annotation { "Feature Type Name" : "Feature", "Feature Type Description" : "" }
export const myFeature = defineFeature(function(context is Context, id is Id, definition is map)
    precondition{}
    {
        {
            var Q0;
            Q0=qCreatedBy(makeId("Top.planeOp"),FACE);
            var sketch = newSketch(context, id + "F0", { "sketchPlane" : qUnion([Q0])});
            skLineSegment(sketch, "E0.left", {"start": v(152.4, 161.9) * mm, "end": v(152.4, -3.62) * mm});
            skLineSegment(sketch, "E0.right", {"start": v(-152.4, 161.9) * mm, "end": v(-152.4, -3.62) * mm});
            skPoint(sketch, "E0.middle", {"position": v(0, 0) * mm});
            skLineSegment(sketch, "E1", {"start": v(-88.9, 201.69) * mm, "end": v(0, 230.34) * mm});
            skLineSegment(sketch, "E2", {"start": v(0, 230.34) * mm, "end": v(0, 0) * mm, "construction": true});
            skLineSegment(sketch, "E3.MirrorCS", {"start": v(88.9, 201.69) * mm, "end": v(0, 230.34) * mm});
            skPoint(sketch, "E4.orphan", {"position": v(-88.9, 201.69) * mm});
            skPoint(sketch, "E0.bottom.end.orphan", {"position": v(88.9, 201.69) * mm});
            skPoint(sketch, "E5.orphan", {"position": v(152.4, 236.65) * mm});
            skArc(sketch, "E6", {"start": v(-152.4, -3.62) * mm, "mid": v(-110.76, -140.2) * mm, "end": v(0, -230.34) * mm});
            skArc(sketch, "E7.MirrorCS", {"start": v(152.4, -3.62) * mm, "mid": v(110.76, -140.2) * mm, "end": v(0, -230.34) * mm});
            skPoint(sketch, "E8.orphan", {"position": v(-152.4, -236.65) * mm});
            skPoint(sketch, "E9.orphan", {"position": v(152.4, -224.03) * mm});
            skPoint(sketch, "E10.orphan", {"position": v(-152.4, 181.18) * mm});
            skPoint(sketch, "E11.center.orphan", {"position": v(-152.4, 224.03) * mm});
            skPoint(sketch, "E12.MirrorCS.center.orphan", {"position": v(147.26, 182.37) * mm});
            skArc(sketch, "E13", {"start": v(-113.58, 176.71) * mm, "mid": v(-98.53, 186.52) * mm, "end": v(-88.9, 201.69) * mm});
            skArc(sketch, "E14.MirrorCS", {"start": v(113.58, 176.71) * mm, "mid": v(98.53, 186.52) * mm, "end": v(88.9, 201.69) * mm});
            skLineSegment(sketch, "E15", {"start": v(-152.4, 161.9) * mm, "end": v(-113.58, 176.71) * mm});
            skLineSegment(sketch, "E16.MirrorCS", {"start": v(152.4, 161.9) * mm, "end": v(113.58, 176.71) * mm});
            skPoint(sketch, "E17.orphan", {"position": v(152.4, 181.18) * mm});
            skSolve(sketch);
        }
        {
            var Q0;
            Q0=makeQuery(id+"F0.imprint","IMPRINT",FACE,{"disambiguationData":[TD([[makeQuery(id+"F0.imprint","IMPRINT",EDGE,{"derivedFrom":sQuery(id+"F0.wireOp",EDGE,"E0.left")}),-1.0]])]});
            extrude(context, id + "F1", {"entities" : qUnion([Q0]), "depth" : 25.4 * mm, "offsetDistance" : 25.4 * mm});
        }
        {
            var Q0;
            Q0=makeQuery(id+"F1.opExtrude","CAP_FACE",FACE,{"disambiguationData":[OSD([sQuery(id+"F0.wireOp",EDGE,"E0.left"),sQuery(id+"F0.wireOp",EDGE,"E0.right"),sQuery(id+"F0.wireOp",EDGE,"E1"),sQuery(id+"F0.wireOp",EDGE,"E3.MirrorCS"),sQuery(id+"F0.wireOp",EDGE,"E6"),sQuery(id+"F0.wireOp",EDGE,"E7.MirrorCS"),sQuery(id+"F0.wireOp",EDGE,"E13"),sQuery(id+"F0.wireOp",EDGE,"E14.MirrorCS"),sQuery(id+"F0.wireOp",EDGE,"E15"),sQuery(id+"F0.wireOp",EDGE,"E16.MirrorCS")])],"isStart":false});
            var sketch = newSketch(context, id + "F2", { "sketchPlane" : qUnion([Q0])});
            skText(sketch, "E18", { "text": "THANK YOU ", "fontName": "RobotoSlab-Regular.ttf"});
            skText(sketch, "E19", { "text": "FOR YOUR DEDICATION", "fontName": "OpenSans-Bold.ttf"});
            skText(sketch, "E20", { "text": "GLENN DODGE", "fontName": "RobotoSlab-Bold.ttf"});
            skText(sketch, "E21", { "text": "501", "fontName": "RobotoSlab-Bold.ttf"});
            skText(sketch, "E22", { "text": "PK", "fontName": "RobotoSlab-Bold.ttf"});
            const initialGuessF2  = {"E18": [-0.13322, 0.12096, 1, 0, 0.03185], "E19": [-0.13322, 0.09164, 1, 0, 0.01662], "E20": [-0.13322, 0.0518, 1, 0, 0.02715], "E21": [-0.02679, 0.18843, 1, 0, 0.0254], "E22": [-0.02221, -0.1981, 1, 0, 0.0254]};
            skSetInitialGuess(sketch, initialGuessF2);
            skSolve(sketch);
        }
        {
            var Q0;
            Q0 = qSketchRegion(id + "F2", true);
            extrude(context, id + "F3", {"entities" : qUnion([Q0]), "operationType" : NewBodyOperationType.REMOVE, "oppositeDirection" : true, "depth" : 2.54 * mm, "offsetDistance" : 25.4 * mm});
        }
        {
            var Q0;
            {var subQ0=sQuery(id+"F0.wireOp",EDGE,"E16.MirrorCS");var subQ1=sQuery(id+"F0.wireOp",EDGE,"E13");var subQ2=sQuery(id+"F0.wireOp",EDGE,"E7.MirrorCS");var subQ3=sQuery(id+"F0.wireOp",EDGE,"E6");var subQ4=sQuery(id+"F0.wireOp",EDGE,"E3.MirrorCS");var subQ5=sQuery(id+"F0.wireOp",EDGE,"E1");var subQ6=sQuery(id+"F0.wireOp",EDGE,"E0.right");var subQ7=sQuery(id+"F0.wireOp",EDGE,"E0.left");var subQ8=sQuery(id+"F0.wireOp",EDGE,"E14.MirrorCS");var subQ9=sQuery(id+"F0.wireOp",EDGE,"E15");Q0=makeQuery(id+"F3.boolean.opBoolean","SPLIT",FACE,{"disambiguationData":[TD([makeQuery(id+"F1.opExtrude","SWEPT_FACE",FACE,{"disambiguationData":[OSD([subQ7])]})])],"derivedFrom":makeQuery(id+"F1.opExtrude","CAP_FACE",FACE,{"disambiguationData":[OSD([subQ7,subQ6,subQ5,subQ4,subQ3,subQ2,subQ1,subQ8,subQ9,subQ0])],"isStart":false})});}
            var sketch = newSketch(context, id + "F4", { "sketchPlane" : qUnion([Q0])});
            skFitSpline(sketch, "E23", {"points": [v(-109.55, 14.42) * mm, v(-110.76, 15.54) * mm, v(-112.72, 16.6) * mm, v(-115.35, 17.1) * mm, v(-118.94, 16.49) * mm, v(-122.25, 14.7) * mm, v(-124.55, 12.17) * mm, v(-126.12, 9.2) * mm, v(-126.62, 6.73) * mm, v(-126.57, 3.31) * mm, v(-126.06, 0.85) * mm, v(-124.38, -2.24) * mm, v(-121.58, -4.93) * mm, v(-118.55, -6.44) * mm, v(-114.74, -6.72) * mm, v(-111.65, -5.82) * mm, v(-109.52, -4.03) * mm, v(-107.11, 1.91) * mm], "startDerivative": vector(-26.95, 27.22) * mm, "endDerivative": vector(26.9, 83.07) * mm});
            skArc(sketch, "E24.0.endCap", {"start": v(-102.57, -3.35) * mm, "mid": v(-105.74, -6.82) * mm, "end": v(-109.54, -4.05) * mm});
            skLineSegment(sketch, "E24.0.left", {"start": v(-102.4, 13.1) * mm, "end": v(-102.57, -3.35) * mm});
            skArc(sketch, "E25", {"start": v(-102.4, 13.1) * mm, "mid": v(-105.42, 16.76) * mm, "end": v(-109.55, 14.42) * mm});
            skFitSpline(sketch, "E26", {"points": [v(-115.26, 10.83) * mm, v(-116.62, 10.46) * mm, v(-118.42, 8.91) * mm, v(-119.3, 6.2) * mm, v(-119.24, 3.33) * mm, v(-118.27, 1) * mm, v(-116.48, -0.21) * mm, v(-114.1, -0.4) * mm, v(-111.72, 0.71) * mm, v(-110.36, 2.36) * mm, v(-109.78, 4.75) * mm, v(-110.27, 8.09) * mm, v(-111.58, 9.78) * mm, v(-113.8, 10.75) * mm, v(-115.26, 10.83) * mm]});
            skLineSegment(sketch, "E27", {"start": v(-94.4, 7.6) * mm, "end": v(-85.17, 7.5) * mm});
            skArc(sketch, "E28", {"start": v(-85.17, 7.5) * mm, "mid": v(-89.74, 11.72) * mm, "end": v(-94.4, 7.6) * mm});
            skLineSegment(sketch, "E29", {"start": v(-94.22, 2.92) * mm, "end": v(-81.56, 2.92) * mm});
            skFitSpline(sketch, "E30", {"points": [v(-81.56, 2.92) * mm, v(-79.2, 3.4) * mm, v(-78.42, 4.75) * mm, v(-78.23, 7.87) * mm, v(-79.06, 10.09) * mm, v(-80.45, 12.3) * mm, v(-82.85, 14.7) * mm, v(-86.27, 16.65) * mm, v(-90.34, 17.02) * mm, v(-94.5, 16.1) * mm, v(-97.45, 14.43) * mm, v(-100.04, 11.66) * mm, v(-101.52, 7.87) * mm, v(-101.92, 4.21) * mm, v(-101.4, 1.18) * mm, v(-99.9, -1.8) * mm, v(-97.9, -3.85) * mm, v(-95.53, -5.39) * mm, v(-92.21, -6.56) * mm, v(-87.52, -6.69) * mm, v(-83.16, -5.71) * mm, v(-79.9, -3.89) * mm, v(-78.46, -2.32) * mm, v(-78.73, -0.1) * mm, v(-81.56, 1.06) * mm, v(-84.46, 0.02) * mm, v(-87.13, -1.02) * mm, v(-89.93, -1.09) * mm, v(-92.21, -0.04) * mm, v(-93.58, 1.26) * mm, v(-94.22, 2.92) * mm], "startDerivative": vector(116.89, 0) * mm, "endDerivative": vector(-21.57, 62.43) * mm});
            skArc(sketch, "E31.0.startCap", {"start": v(-77.05, 13.54) * mm, "mid": v(-74.16, 16.82) * mm, "end": v(-70.55, 14.35) * mm});
            skArc(sketch, "E31.0.endCap", {"start": v(-70.45, -3.57) * mm, "mid": v(-73.75, -6.87) * mm, "end": v(-77.05, -3.57) * mm});
            skLineSegment(sketch, "E31.0.left", {"start": v(-70.45, 6.87) * mm, "end": v(-70.45, -3.57) * mm});
            skLineSegment(sketch, "E31.0.right", {"start": v(-77.05, 13.54) * mm, "end": v(-77.05, -3.57) * mm});
            skFitSpline(sketch, "E32", {"points": [v(-70.55, 14.35) * mm, v(-68.5, 16.21) * mm, v(-66.37, 16.92) * mm, v(-64.41, 17.15) * mm, v(-64.41, 15.27) * mm, v(-62.92, 11.74) * mm, v(-63.31, 11.03) * mm, v(-64.73, 10.64) * mm, v(-66.45, 10.09) * mm, v(-68.96, 9.15) * mm, v(-70.45, 6.87) * mm], "startDerivative": vector(17.8, 19.08) * mm, "endDerivative": vector(-10.39, -23.26) * mm});
            skCircle(sketch, "E33", {"center": v(-55.46, 16.5) * mm, "radius": 6.35 * mm});
            skArc(sketch, "E34", {"start": v(-60.77, 9.77) * mm, "mid": v(-55.99, 7.95) * mm, "end": v(-51.02, 9.17) * mm});
            skFitSpline(sketch, "E35", {"points": [v(-62.16, 21.84) * mm, v(-62.1, 24.08) * mm, v(-61.24, 26.58) * mm, v(-60.23, 29.07) * mm, v(-59.15, 31.31) * mm, v(-57.27, 33.71) * mm, v(-55.04, 36.54) * mm, v(-51.7, 39.03) * mm, v(-47.84, 40.91) * mm, v(-41.5, 42.63) * mm, v(-34.9, 42.63) * mm, v(-29.5, 41.6) * mm, v(-24.61, 39.11) * mm, v(-20.15, 35.34) * mm, v(-15.95, 27.54) * mm], "startDerivative": vector(-2.37, 43.6) * mm, "endDerivative": vector(38.1, -85.11) * mm});
            skFitSpline(sketch, "E36", {"points": [v(-15.95, 27.54) * mm, v(-18.27, 28.4) * mm, v(-20.5, 28.31) * mm, v(-22.9, 27.54) * mm, v(-24.1, 25.53) * mm, v(-25.41, 29.2) * mm, v(-27.64, 33.03) * mm, v(-30.1, 35.6) * mm, v(-33.01, 37.4) * mm, v(-36.87, 37.57) * mm, v(-40.98, 35.94) * mm, v(-44.41, 32.85) * mm, v(-47.5, 27.54) * mm, v(-49.27, 22.44) * mm], "startDerivative": vector(-37.27, 17.9) * mm, "endDerivative": vector(-16.52, -54.42) * mm});
            skCircle(sketch, "E37", {"center": v(-55.23, -7.55) * mm, "radius": 6.35 * mm});
            skArc(sketch, "E38", {"start": v(-60.06, -14.63) * mm, "mid": v(-55.04, -16.12) * mm, "end": v(-50.1, -14.41) * mm});
            skLineSegment(sketch, "E39", {"start": v(-60.77, 9.77) * mm, "end": v(-60.77, -1) * mm});
            skLineSegment(sketch, "E40", {"start": v(-51.02, 9.17) * mm, "end": v(-51.02, -0.08) * mm});
            skArc(sketch, "E41.trimOffspring", {"start": v(-49.27, 22.44) * mm, "mid": v(-55.85, 25.07) * mm, "end": v(-62.16, 21.84) * mm});
            skLineSegment(sketch, "E42", {"start": v(-60.06, -14.63) * mm, "end": v(-60.06, -30.38) * mm});
            skLineSegment(sketch, "E43", {"start": v(-59.43, -31.02) * mm, "end": v(-50.74, -31.11) * mm});
            skLineSegment(sketch, "E44", {"start": v(-50.1, -30.48) * mm, "end": v(-50.1, -14.41) * mm});
            skArc(sketch, "E45.filletArc", {"start": v(-60.06, -30.38) * mm, "mid": v(-59.87, -30.83) * mm, "end": v(-59.43, -31.02) * mm});
            skArc(sketch, "E46.filletArc", {"start": v(-50.74, -31.11) * mm, "mid": v(-50.28, -30.93) * mm, "end": v(-50.1, -30.48) * mm});
            skArc(sketch, "E47.trimOffspring", {"start": v(-51.02, -0.08) * mm, "mid": v(-56.04, 0.99) * mm, "end": v(-60.77, -1) * mm});
            skFitSpline(sketch, "E48", {"points": [v(-47.09, 18.63) * mm, v(-47.52, 21.85) * mm, v(-46.77, 25.6) * mm, v(-44.83, 28.83) * mm, v(-42.58, 31.3) * mm, v(-39.57, 33.12) * mm, v(-35.92, 33.44) * mm, v(-31.84, 32.7) * mm, v(-29.16, 31.08) * mm, v(-27.12, 28.5) * mm, v(-25.18, 24.2) * mm, v(-25.08, 18.84) * mm], "startDerivative": vector(-7.7, 37.27) * mm, "endDerivative": vector(-3.75, -50.87) * mm});
            skFitSpline(sketch, "E49", {"points": [v(-25.08, 18.84) * mm, v(-26.26, 22.5) * mm, v(-27.65, 24.53) * mm, v(-30.12, 26.68) * mm, v(-33.13, 28.18) * mm, v(-36.46, 28.4) * mm, v(-39.79, 27.97) * mm, v(-43.97, 25.17) * mm, v(-45.8, 22.38) * mm, v(-47.09, 18.63) * mm], "startDerivative": vector(-9.3, 34.22) * mm, "endDerivative": vector(-10.28, -33.52) * mm});
            skFitSpline(sketch, "E50", {"points": [v(-32.26, 14.42) * mm, v(-33.46, 15.54) * mm, v(-35.42, 16.6) * mm, v(-38.06, 17.1) * mm, v(-41.64, 16.49) * mm, v(-44.95, 14.7) * mm, v(-47.25, 12.17) * mm, v(-48.82, 9.2) * mm, v(-49.33, 6.73) * mm, v(-49.27, 3.31) * mm, v(-48.76, 0.85) * mm, v(-47.08, -2.24) * mm, v(-44.28, -4.93) * mm, v(-41.25, -6.44) * mm, v(-37.44, -6.72) * mm, v(-34.36, -5.82) * mm, v(-32.23, -4.03) * mm, v(-29.82, 1.91) * mm], "startDerivative": vector(-26.95, 27.22) * mm, "endDerivative": vector(26.9, 83.07) * mm});
            skArc(sketch, "E51.0.endCap", {"start": v(-25.28, -3.35) * mm, "mid": v(-28.45, -6.82) * mm, "end": v(-32.24, -4.05) * mm});
            skLineSegment(sketch, "E51.0.left", {"start": v(-25.1, 13.1) * mm, "end": v(-25.28, -3.35) * mm});
            skArc(sketch, "E52", {"start": v(-25.1, 13.1) * mm, "mid": v(-28.12, 16.76) * mm, "end": v(-32.26, 14.42) * mm});
            skFitSpline(sketch, "E53", {"points": [v(-37.96, 10.83) * mm, v(-39.33, 10.46) * mm, v(-41.12, 8.91) * mm, v(-42, 6.2) * mm, v(-41.95, 3.33) * mm, v(-40.98, 1) * mm, v(-39.18, -0.21) * mm, v(-36.8, -0.4) * mm, v(-34.42, 0.71) * mm, v(-33.07, 2.36) * mm, v(-32.48, 4.75) * mm, v(-32.97, 8.09) * mm, v(-34.28, 9.78) * mm, v(-36.51, 10.75) * mm, v(-37.96, 10.83) * mm]});
            skLineSegment(sketch, "E54", {"start": v(-15.57, 23.87) * mm, "end": v(-15.57, -9.23) * mm});
            skLineSegment(sketch, "E55", {"start": v(-15.57, -9.23) * mm, "end": v(-10.68, -9.28) * mm});
            skLineSegment(sketch, "E56", {"start": v(-10.68, -9.28) * mm, "end": v(-10.68, -12.75) * mm});
            skLineSegment(sketch, "E57", {"start": v(-10.68, -12.75) * mm, "end": v(-11.18, -14.54) * mm});
            skLineSegment(sketch, "E58", {"start": v(-11.18, -14.54) * mm, "end": v(-15.43, -14.5) * mm});
            skLineSegment(sketch, "E59", {"start": v(-15.43, -14.5) * mm, "end": v(-15.43, -24.4) * mm});
            skFitSpline(sketch, "E60", {"points": [v(-15.43, -24.4) * mm, v(-14.75, -25.56) * mm, v(-13.67, -26.18) * mm, v(-11.58, -25.79) * mm], "startDerivative": vector(1.89, -4.02) * mm, "endDerivative": vector(5.77, 1.79) * mm});
            skLineSegment(sketch, "E61", {"start": v(-11.58, -25.79) * mm, "end": v(-10.4, -25.79) * mm});
            skLineSegment(sketch, "E62", {"start": v(-10.4, -25.79) * mm, "end": v(-10.4, -28.5) * mm});
            skFitSpline(sketch, "E63", {"points": [v(-10.4, -28.5) * mm, v(-10.4, -30.28) * mm, v(-11.74, -31.43) * mm, v(-14.24, -31.53) * mm, v(-17.26, -31.95) * mm, v(-19.34, -31.64) * mm, v(-21.74, -31.01) * mm, v(-24.65, -28.5) * mm, v(-25.07, -25.07) * mm, v(-24.96, -14.66) * mm], "startDerivative": vector(3.8, -22.5) * mm, "endDerivative": vector(0.14, 58.8) * mm});
            skLineSegment(sketch, "E64", {"start": v(-24.96, -14.66) * mm, "end": v(-28.5, -14.66) * mm});
            skLineSegment(sketch, "E65", {"start": v(-28.5, -14.66) * mm, "end": v(-28.04, -9.47) * mm});
            skLineSegment(sketch, "E66", {"start": v(-28.04, -9.47) * mm, "end": v(-24.62, -9.47) * mm});
            skLineSegment(sketch, "E67", {"start": v(-24.62, -9.47) * mm, "end": v(-24.62, -3.97) * mm});
            skArc(sketch, "E68", {"start": v(-23.16, -2.43) * mm, "mid": v(-24.2, -2.91) * mm, "end": v(-24.62, -3.97) * mm});
            skLineSegment(sketch, "E69", {"start": v(-23.16, -2.43) * mm, "end": v(-22.4, -2.4) * mm});
            skLineSegment(sketch, "E70", {"start": v(-22.4, -2.4) * mm, "end": v(-22.4, 23.87) * mm});
            skArc(sketch, "E71", {"start": v(-15.57, 23.87) * mm, "mid": v(-18.99, 26.78) * mm, "end": v(-22.4, 23.87) * mm});
            skLineSegment(sketch, "E72", {"start": v(-126.11, -15.94) * mm, "end": v(-126.11, -10.96) * mm});
            skFitSpline(sketch, "E73", {"points": [v(-126.11, -10.96) * mm, v(-126.11, -10.25) * mm, v(-123.78, -9.73) * mm, v(-120.03, -9.02) * mm, v(-115.64, -8.9) * mm, v(-112.14, -8.96) * mm, v(-109.23, -9.6) * mm, v(-106.39, -10.96) * mm, v(-104.53, -14.07) * mm], "startDerivative": vector(-3.73, 12.95) * mm, "endDerivative": vector(10.17, -25.55) * mm});
            skLineSegment(sketch, "E74", {"start": v(-104.53, -14.07) * mm, "end": v(-104.53, -31.05) * mm});
            skLineSegment(sketch, "E75", {"start": v(-104.53, -31.05) * mm, "end": v(-114.02, -31.05) * mm});
            skLineSegment(sketch, "E76", {"start": v(-114.02, -31.05) * mm, "end": v(-114.02, -29.46) * mm});
            skFitSpline(sketch, "E77", {"points": [v(-114.02, -29.46) * mm, v(-116.08, -30.46) * mm, v(-117.59, -31) * mm, v(-119.42, -31.43) * mm, v(-123.2, -31.27) * mm, v(-127, -29.46) * mm, v(-128.76, -26.43) * mm, v(-128.76, -22.7) * mm, v(-127.22, -20.2) * mm, v(-124.66, -18.38) * mm, v(-121.58, -17.35) * mm, v(-117.92, -16.77) * mm, v(-114.02, -16.1) * mm, v(-114.02, -15.3) * mm, v(-115.14, -14.28) * mm, v(-118.14, -14.06) * mm, v(-120.85, -14.42) * mm, v(-123.63, -15.08) * mm, v(-126.11, -15.94) * mm], "startDerivative": vector(-42.37, -21.84) * mm, "endDerivative": vector(-44.8, -16.78) * mm});
            skLineSegment(sketch, "E78", {"start": v(-114.04, -20.2) * mm, "end": v(-114.04, -24.68) * mm});
            skFitSpline(sketch, "E79", {"points": [v(-114.04, -24.68) * mm, v(-115.06, -25.33) * mm, v(-116.3, -25.7) * mm, v(-117.92, -25.63) * mm, v(-119.39, -24.68) * mm, v(-119.77, -23.32) * mm, v(-119.33, -21.87) * mm, v(-117.92, -21.16) * mm, v(-115.94, -20.8) * mm, v(-114.04, -20.2) * mm], "startDerivative": vector(-10.07, -7.34) * mm, "endDerivative": vector(14.7, 5.52) * mm});
            skLineSegment(sketch, "E80", {"start": v(-83.8, -9.48) * mm, "end": v(-84.3, -15.02) * mm});
            skLineSegment(sketch, "E81", {"start": v(-103.2, -24.69) * mm, "end": v(-103.26, -29.94) * mm});
            skFitSpline(sketch, "E82", {"points": [v(-103.2, -24.69) * mm, v(-102.92, -24.45) * mm, v(-102.32, -24.35) * mm, v(-101.43, -25) * mm, v(-99.57, -25.97) * mm, v(-97.95, -26.39) * mm, v(-96.1, -26.7) * mm, v(-93.95, -26.57) * mm, v(-92.98, -26.07) * mm, v(-92.51, -25.23) * mm, v(-92.88, -24.32) * mm, v(-93.61, -23.87) * mm, v(-94.9, -23.38) * mm, v(-96.64, -22.72) * mm, v(-98.03, -22.15) * mm, v(-100.1, -21.29) * mm, v(-101.64, -19.8) * mm, v(-102.8, -17.83) * mm, v(-103.2, -15.6) * mm, v(-102.36, -12.6) * mm, v(-100.22, -10.29) * mm, v(-96, -8.82) * mm, v(-88.63, -8.69) * mm, v(-83.8, -9.48) * mm], "startDerivative": vector(12.94, 13.12) * mm, "endDerivative": vector(65.15, -13.59) * mm});
            skFitSpline(sketch, "E83", {"points": [v(-84.3, -15.02) * mm, v(-85.84, -14.4) * mm, v(-87.52, -13.68) * mm, v(-89.05, -13.35) * mm, v(-91.15, -13.35) * mm, v(-92.8, -13.88) * mm, v(-93.32, -15.02) * mm, v(-92.21, -16.04) * mm, v(-89.38, -17.03) * mm, v(-87.52, -17.68) * mm, v(-85.31, -18.8) * mm, v(-83.8, -20.37) * mm, v(-82.69, -22.15) * mm, v(-82.43, -25.16) * mm, v(-83.8, -28.18) * mm, v(-85.58, -29.7) * mm, v(-88.07, -30.87) * mm, v(-91.68, -31.53) * mm, v(-95.1, -31.8) * mm, v(-98.5, -31.2) * mm, v(-101.06, -30.68) * mm, v(-103.26, -29.94) * mm], "startDerivative": vector(-38, 14.53) * mm, "endDerivative": vector(-45.82, 17.03) * mm});
            skLineSegment(sketch, "E84", {"start": v(-63, -12.25) * mm, "end": v(-63.24, -15.02) * mm});
            skLineSegment(sketch, "E85", {"start": v(-82.16, -24.69) * mm, "end": v(-82.21, -29.94) * mm});
            skFitSpline(sketch, "E86", {"points": [v(-82.16, -24.69) * mm, v(-81.87, -24.45) * mm, v(-81.27, -24.35) * mm, v(-80.38, -25) * mm, v(-78.53, -25.97) * mm, v(-76.9, -26.39) * mm, v(-75.05, -26.7) * mm, v(-72.9, -26.57) * mm, v(-71.93, -26.07) * mm, v(-71.46, -25.23) * mm, v(-71.83, -24.32) * mm, v(-72.56, -23.87) * mm, v(-73.84, -23.38) * mm, v(-75.6, -22.72) * mm, v(-76.98, -22.15) * mm, v(-79.05, -21.29) * mm, v(-80.6, -19.8) * mm, v(-81.74, -17.83) * mm, v(-82.16, -15.6) * mm, v(-81.31, -12.6) * mm, v(-79.17, -10.29) * mm, v(-74.95, -8.82) * mm, v(-67.59, -8.69) * mm, v(-62.74, -9.48) * mm], "startDerivative": vector(12.94, 13.12) * mm, "endDerivative": vector(65.15, -13.59) * mm});
            skFitSpline(sketch, "E87", {"points": [v(-63.24, -15.02) * mm, v(-64.8, -14.4) * mm, v(-66.47, -13.68) * mm, v(-68, -13.35) * mm, v(-70.1, -13.35) * mm, v(-71.75, -13.88) * mm, v(-72.27, -15.02) * mm, v(-71.16, -16.04) * mm, v(-68.33, -17.03) * mm, v(-66.47, -17.68) * mm, v(-64.27, -18.8) * mm, v(-62.74, -20.37) * mm, v(-61.64, -22.15) * mm, v(-61.38, -25.16) * mm, v(-62.74, -28.18) * mm, v(-64.53, -29.7) * mm, v(-67.02, -30.87) * mm, v(-70.63, -31.53) * mm, v(-74.04, -31.8) * mm, v(-77.46, -31.2) * mm, v(-80.01, -30.68) * mm, v(-82.21, -29.94) * mm], "startDerivative": vector(-38, 14.53) * mm, "endDerivative": vector(-45.82, 17.03) * mm});
            skLineSegment(sketch, "E88", {"start": v(-63, -12.25) * mm, "end": v(-64.62, -9.1) * mm});
            skLineSegment(sketch, "E89", {"start": v(-29.29, -9.36) * mm, "end": v(-29.79, -14.9) * mm});
            skLineSegment(sketch, "E90", {"start": v(-48.7, -24.57) * mm, "end": v(-48.76, -29.83) * mm});
            skFitSpline(sketch, "E91", {"points": [v(-48.7, -24.57) * mm, v(-48.42, -24.33) * mm, v(-47.82, -24.23) * mm, v(-46.93, -24.88) * mm, v(-45.07, -25.85) * mm, v(-43.45, -26.27) * mm, v(-41.6, -26.58) * mm, v(-39.45, -26.45) * mm, v(-38.48, -25.96) * mm, v(-38, -25.12) * mm, v(-38.37, -24.2) * mm, v(-39.1, -23.76) * mm, v(-40.39, -23.26) * mm, v(-42.14, -22.6) * mm, v(-43.53, -22.03) * mm, v(-45.6, -21.17) * mm, v(-47.14, -19.68) * mm, v(-48.29, -17.72) * mm, v(-48.7, -15.49) * mm, v(-47.86, -12.49) * mm, v(-45.72, -10.17) * mm, v(-41.5, -8.7) * mm, v(-34.13, -8.57) * mm, v(-29.29, -9.36) * mm], "startDerivative": vector(12.94, 13.12) * mm, "endDerivative": vector(65.15, -13.59) * mm});
            skFitSpline(sketch, "E92", {"points": [v(-29.79, -14.9) * mm, v(-31.33, -14.29) * mm, v(-33.02, -13.56) * mm, v(-34.55, -13.24) * mm, v(-36.65, -13.24) * mm, v(-38.3, -13.76) * mm, v(-38.82, -14.9) * mm, v(-37.7, -15.93) * mm, v(-34.88, -16.91) * mm, v(-33.02, -17.56) * mm, v(-30.81, -18.68) * mm, v(-29.29, -20.26) * mm, v(-28.19, -22.03) * mm, v(-27.92, -25.05) * mm, v(-29.29, -28.07) * mm, v(-31.07, -29.58) * mm, v(-33.57, -30.76) * mm, v(-37.18, -31.41) * mm, v(-40.59, -31.68) * mm, v(-44, -31.08) * mm, v(-46.56, -30.56) * mm, v(-48.76, -29.83) * mm], "startDerivative": vector(-38, 14.53) * mm, "endDerivative": vector(-45.82, 17.03) * mm});
            skLineSegment(sketch, "E93", {"start": v(23.64, 6.1) * mm, "end": v(23.64, -12.36) * mm});
            skLineSegment(sketch, "E94", {"start": v(23.64, -12.36) * mm, "end": v(40.74, -12.36) * mm});
            skLineSegment(sketch, "E95", {"start": v(40.74, -12.36) * mm, "end": v(40.74, -7.23) * mm});
            skLineSegment(sketch, "E96", {"start": v(40.74, -7.23) * mm, "end": v(31.4, -7.23) * mm});
            skLineSegment(sketch, "E97", {"start": v(31.4, -7.23) * mm, "end": v(31.4, -5.24) * mm});
            skLineSegment(sketch, "E98", {"start": v(31.4, -5.24) * mm, "end": v(38.9, -5.24) * mm});
            skLineSegment(sketch, "E99", {"start": v(38.9, -5.24) * mm, "end": v(38.9, -1.07) * mm});
            skLineSegment(sketch, "E100", {"start": v(38.9, -1.07) * mm, "end": v(31.33, -1.07) * mm});
            skLineSegment(sketch, "E101", {"start": v(31.33, -1.07) * mm, "end": v(31.33, 0.91) * mm});
            skLineSegment(sketch, "E102", {"start": v(31.33, 0.91) * mm, "end": v(40.32, 0.91) * mm});
            skLineSegment(sketch, "E103", {"start": v(40.32, 0.91) * mm, "end": v(40.32, 6.1) * mm});
            skLineSegment(sketch, "E104", {"start": v(40.32, 6.1) * mm, "end": v(23.64, 6.1) * mm});
            skLineSegment(sketch, "E105.bottom", {"start": v(1.26, 5.93) * mm, "end": v(8.98, 5.93) * mm});
            skLineSegment(sketch, "E105.top", {"start": v(1.26, -12.25) * mm, "end": v(8.98, -12.25) * mm});
            skLineSegment(sketch, "E105.left", {"start": v(1.26, 5.93) * mm, "end": v(1.26, -12.25) * mm});
            skLineSegment(sketch, "E105.right", {"start": v(8.98, 1.6) * mm, "end": v(8.98, -2.33) * mm});
            skFitSpline(sketch, "E106", {"points": [v(8.98, 5.93) * mm, v(14.34, 5.93) * mm, v(16.49, 5.67) * mm, v(18.12, 5.2) * mm, v(19.63, 4.39) * mm, v(20.57, 3.24) * mm, v(21.11, 2.09) * mm, v(21.33, 0.5) * mm, v(21.3, -1.2) * mm, v(20.92, -2.65) * mm, v(20.11, -3.88) * mm, v(18.74, -4.96) * mm, v(17.64, -5.39) * mm], "startDerivative": vector(42.38, 0.73) * mm, "endDerivative": vector(-16, -4.77) * mm});
            skFitSpline(sketch, "E107", {"points": [v(17.64, -5.39) * mm, v(18.38, -5.8) * mm, v(19.34, -6.55) * mm, v(20.06, -7.94) * mm, v(20.57, -9.08) * mm, v(21.88, -12.36) * mm], "startDerivative": vector(4.88, -2.66) * mm, "endDerivative": vector(4.84, -12.6) * mm});
            skLineSegment(sketch, "E108", {"start": v(21.88, -12.36) * mm, "end": v(14.05, -12.36) * mm});
            skLineSegment(sketch, "E109", {"start": v(14.05, -12.36) * mm, "end": v(12.73, -9.05) * mm});
            skFitSpline(sketch, "E110", {"points": [v(12.73, -9.05) * mm, v(12.27, -7.8) * mm, v(11.85, -6.85) * mm, v(11.08, -6.37) * mm, v(9.33, -6.3) * mm, v(8.98, -6.3) * mm], "startDerivative": vector(-2.08, 5.74) * mm, "endDerivative": vector(-2.94, 0.06) * mm});
            skFitSpline(sketch, "E111", {"points": [v(8.98, 1.6) * mm, v(12.73, 1.67) * mm, v(13.68, 0.92) * mm, v(13.99, -0.1) * mm, v(13.78, -1.37) * mm, v(13.31, -1.99) * mm, v(12.73, -2.17) * mm, v(11.52, -2.33) * mm, v(9.83, -2.3) * mm, v(8.98, -2.33) * mm], "startDerivative": vector(23.7, 2.7) * mm, "endDerivative": vector(-9.58, -0.43) * mm});
            skLineSegment(sketch, "E112.trimOffspring", {"start": v(8.98, -6.3) * mm, "end": v(8.98, -12.25) * mm});
            skLineSegment(sketch, "E113.bottom", {"start": v(100.4, 10.3) * mm, "end": v(108.14, 10.3) * mm});
            skLineSegment(sketch, "E113.top", {"start": v(100.4, -12.15) * mm, "end": v(108.14, -12.15) * mm});
            skLineSegment(sketch, "E113.left", {"start": v(100.4, 10.3) * mm, "end": v(100.4, -1.96) * mm});
            skLineSegment(sketch, "E113.right", {"start": v(108.14, 10.3) * mm, "end": v(108.14, -7.34) * mm});
            skLineSegment(sketch, "E114", {"start": v(108.14, -12.15) * mm, "end": v(113.85, -12.15) * mm});
            skLineSegment(sketch, "E115", {"start": v(113.85, -12.15) * mm, "end": v(113.85, -7.34) * mm});
            skLineSegment(sketch, "E116", {"start": v(113.85, -7.34) * mm, "end": v(108.14, -7.34) * mm});
            skLineSegment(sketch, "E117", {"start": v(98.03, -8.5) * mm, "end": v(98.03, -12.16) * mm});
            skLineSegment(sketch, "E118", {"start": v(98.03, -12.16) * mm, "end": v(96.38, -12.16) * mm});
            skFitSpline(sketch, "E119", {"points": [v(98.03, -8.5) * mm, v(98.76, -7.42) * mm, v(99.57, -6.2) * mm, v(100.4, -4.7) * mm], "startDerivative": vector(2.32, 3.42) * mm, "endDerivative": vector(2.26, 4.32) * mm});
            skFitSpline(sketch, "E120", {"points": [v(100.4, -1.96) * mm, v(98.69, -2.5) * mm, v(97.5, -3.17) * mm, v(96.26, -4.65) * mm, v(94.53, -7.27) * mm], "startDerivative": vector(-7.59, -2.16) * mm, "endDerivative": vector(-5.73, -8.86) * mm});
            skFitSpline(sketch, "E121", {"points": [v(94.53, -7.27) * mm, v(91.8, -7.27) * mm, v(89.82, -5.74) * mm, v(89.55, -3.17) * mm, v(89.68, -0.9) * mm, v(90.8, 0.5) * mm, v(93.43, 0.91) * mm], "startDerivative": vector(-15.66, -2.03) * mm, "endDerivative": vector(16.66, 0.52) * mm});
            skLineSegment(sketch, "E122", {"start": v(93.43, 0.91) * mm, "end": v(98.16, 0.91) * mm});
            skLineSegment(sketch, "E123", {"start": v(98.16, 0.91) * mm, "end": v(98.16, 5.83) * mm});
            skLineSegment(sketch, "E124", {"start": v(98.16, 5.83) * mm, "end": v(90.09, 5.83) * mm});
            skFitSpline(sketch, "E125", {"points": [v(90.09, 5.83) * mm, v(88.9, 5.83) * mm, v(86.44, 5.1) * mm, v(84.7, 4.12) * mm, v(83.07, 2.38) * mm, v(82.18, 0.32) * mm, v(81.78, -1.45) * mm, v(81.86, -4.71) * mm, v(82.3, -7.06) * mm, v(83.83, -9.6) * mm, v(85.55, -10.99) * mm, v(88.86, -12.18) * mm, v(92.02, -12.23) * mm], "startDerivative": vector(-17.73, 2.05) * mm, "endDerivative": vector(32.25, 2.73) * mm});
            skLineSegment(sketch, "E126.trimOffspring", {"start": v(100.4, -4.7) * mm, "end": v(100.4, -12.15) * mm});
            skLineSegment(sketch, "E127", {"start": v(116.03, 6.1) * mm, "end": v(116.03, -12.36) * mm});
            skLineSegment(sketch, "E128", {"start": v(116.03, -12.36) * mm, "end": v(133.13, -12.36) * mm});
            skLineSegment(sketch, "E129", {"start": v(133.13, -12.36) * mm, "end": v(133.13, -7.23) * mm});
            skLineSegment(sketch, "E130", {"start": v(133.13, -7.23) * mm, "end": v(123.8, -7.23) * mm});
            skLineSegment(sketch, "E131", {"start": v(123.8, -7.23) * mm, "end": v(123.8, -5.24) * mm});
            skLineSegment(sketch, "E132", {"start": v(123.8, -5.24) * mm, "end": v(131.28, -5.24) * mm});
            skLineSegment(sketch, "E133", {"start": v(131.28, -5.24) * mm, "end": v(131.28, -1.07) * mm});
            skLineSegment(sketch, "E134", {"start": v(131.28, -1.07) * mm, "end": v(123.72, -1.07) * mm});
            skLineSegment(sketch, "E135", {"start": v(123.72, -1.07) * mm, "end": v(123.72, 0.91) * mm});
            skLineSegment(sketch, "E136", {"start": v(123.72, 0.91) * mm, "end": v(132.7, 0.91) * mm});
            skLineSegment(sketch, "E137", {"start": v(132.7, 0.91) * mm, "end": v(132.7, 6.1) * mm});
            skLineSegment(sketch, "E138", {"start": v(132.7, 6.1) * mm, "end": v(116.03, 6.1) * mm});
            skLineSegment(sketch, "E139", {"start": v(67.63, -17.63) * mm, "end": v(75.45, -17.63) * mm});
            skLineSegment(sketch, "E140", {"start": v(75.45, -17.63) * mm, "end": v(75.45, -8.1) * mm});
            skLineSegment(sketch, "E141", {"start": v(75.45, -8.1) * mm, "end": v(80.65, 2.38) * mm});
            skLineSegment(sketch, "E142", {"start": v(67.63, -17.63) * mm, "end": v(67.63, -8.1) * mm});
            skLineSegment(sketch, "E143", {"start": v(67.63, -8.1) * mm, "end": v(60.33, 5.64) * mm});
            skLineSegment(sketch, "E144", {"start": v(58.18, 18.08) * mm, "end": v(55.7, 19.28) * mm});
            skLineSegment(sketch, "E145", {"start": v(55.7, 19.28) * mm, "end": v(64.33, 20.93) * mm});
            skLineSegment(sketch, "E146", {"start": v(64.33, 20.93) * mm, "end": v(66.84, 13.06) * mm});
            skLineSegment(sketch, "E147", {"start": v(66.84, 13.06) * mm, "end": v(64.5, 14.5) * mm});
            skLineSegment(sketch, "E148", {"start": v(73.87, 2.69) * mm, "end": v(70.8, 6.24) * mm});
            skLineSegment(sketch, "E149", {"start": v(70.8, 6.24) * mm, "end": v(76.37, 12.34) * mm});
            skLineSegment(sketch, "E150", {"start": v(76.37, 12.34) * mm, "end": v(76.3, 9.6) * mm});
            skLineSegment(sketch, "E151", {"start": v(80.5, 25.01) * mm, "end": v(82.78, 26.56) * mm});
            skLineSegment(sketch, "E152", {"start": v(82.78, 26.56) * mm, "end": v(79.9, 18.26) * mm});
            skLineSegment(sketch, "E153", {"start": v(79.9, 18.26) * mm, "end": v(71.82, 20.02) * mm});
            skLineSegment(sketch, "E154", {"start": v(71.82, 20.02) * mm, "end": v(74.24, 21.34) * mm});
            skLineSegment(sketch, "E155", {"start": v(74.24, 21.34) * mm, "end": v(71.7, 25.98) * mm});
            skLineSegment(sketch, "E156", {"start": v(71.7, 25.98) * mm, "end": v(68.34, 19.89) * mm});
            skLineSegment(sketch, "E157", {"start": v(68.34, 19.89) * mm, "end": v(62.04, 23.37) * mm});
            skLineSegment(sketch, "E158", {"start": v(62.04, 23.37) * mm, "end": v(64.46, 27.74) * mm});
            skFitSpline(sketch, "E159", {"points": [v(64.46, 27.74) * mm, v(65.35, 28.82) * mm, v(67.25, 29.45) * mm, v(77.35, 29.3) * mm, v(77.62, 29.24) * mm, v(78.32, 28.82) * mm, v(79.22, 27.74) * mm, v(80.5, 25.01) * mm], "startDerivative": vector(7.55, 10.2) * mm, "endDerivative": vector(7.62, -17.7) * mm});
            skLineSegment(sketch, "E160", {"start": v(64.5, 14.5) * mm, "end": v(61.62, 9.78) * mm});
            skLineSegment(sketch, "E161", {"start": v(61.62, 9.78) * mm, "end": v(67.02, 9.78) * mm});
            skLineSegment(sketch, "E162", {"start": v(67.02, 9.78) * mm, "end": v(71.9, -2.03) * mm});
            skLineSegment(sketch, "E163", {"start": v(71.9, -2.03) * mm, "end": v(73.87, 2.69) * mm});
            skLineSegment(sketch, "E164", {"start": v(58.18, 18.08) * mm, "end": v(56.6, 15.44) * mm});
            skFitSpline(sketch, "E165", {"points": [v(56.6, 15.44) * mm, v(56.17, 14.66) * mm, v(56.02, 13.29) * mm, v(56.6, 11.82) * mm, v(60.33, 5.64) * mm], "startDerivative": vector(-3.02, -4.47) * mm, "endDerivative": vector(10.8, -16.46) * mm});
            skLineSegment(sketch, "E166", {"start": v(76.3, 9.6) * mm, "end": v(81.52, 9.6) * mm});
            skLineSegment(sketch, "E167", {"start": v(81.52, 9.6) * mm, "end": v(78.06, 15.95) * mm});
            skLineSegment(sketch, "E168", {"start": v(78.06, 15.95) * mm, "end": v(84.5, 19.45) * mm});
            skLineSegment(sketch, "E169", {"start": v(84.5, 19.45) * mm, "end": v(86.64, 15.5) * mm});
            skFitSpline(sketch, "E170", {"points": [v(86.64, 15.5) * mm, v(87.24, 13.95) * mm, v(87.02, 11.95) * mm, v(84.43, 7.8) * mm, v(81.73, 3.42) * mm, v(80.65, 2.38) * mm], "startDerivative": vector(4.81, -9.86) * mm, "endDerivative": vector(-7.04, -5.45) * mm});
            skLineSegment(sketch, "E171", {"start": v(58.26, 0.83) * mm, "end": v(58.26, 5.97) * mm});
            skLineSegment(sketch, "E172", {"start": v(58.26, 5.97) * mm, "end": v(50.7, 5.97) * mm});
            skLineSegment(sketch, "E173", {"start": v(58.26, 0.83) * mm, "end": v(52.5, 0.83) * mm});
            skLineSegment(sketch, "E174", {"start": v(63.63, -7.27) * mm, "end": v(63.63, -12.38) * mm});
            skLineSegment(sketch, "E175", {"start": v(63.63, -12.38) * mm, "end": v(50.76, -12.38) * mm});
            skLineSegment(sketch, "E176", {"start": v(63.63, -7.27) * mm, "end": v(52.62, -7.27) * mm});
            skFitSpline(sketch, "E177", {"points": [v(52.62, -7.27) * mm, v(51.72, -7.27) * mm, v(50.78, -6.57) * mm, v(50.09, -5.47) * mm, v(49.85, -4.24) * mm, v(49.85, -2.68) * mm, v(49.89, -1.33) * mm, v(50.4, -0.3) * mm, v(51.2, 0.42) * mm, v(52.5, 0.83) * mm], "startDerivative": vector(-9.51, -1.43) * mm, "endDerivative": vector(11.9, 2.65) * mm});
            skFitSpline(sketch, "E178", {"points": [v(50.7, 5.97) * mm, v(48.93, 5.86) * mm, v(47.33, 5.43) * mm, v(46.04, 5) * mm, v(45.2, 4.42) * mm, v(44, 3.25) * mm, v(43.06, 1.84) * mm, v(42.4, 0.41) * mm, v(42.1, -1.34) * mm, v(41.93, -2.56) * mm, v(41.87, -4.24) * mm, v(42.2, -6.25) * mm, v(43, -8.37) * mm, v(44.22, -9.88) * mm, v(46.57, -11.56) * mm, v(50.76, -12.38) * mm], "startDerivative": vector(-27.54, -0.28) * mm, "endDerivative": vector(44.63, -4.63) * mm});
            skFitSpline(sketch, "E179", {"points": [v(96.38, -12.16) * mm, v(94.87, -15.6) * mm, v(93.17, -19.8) * mm, v(92.12, -24.1) * mm, v(94.6, -20.84) * mm, v(99.3, -17.18) * mm, v(102.45, -15.74) * mm, v(104.08, -16.12) * mm, v(104.8, -17.56) * mm, v(104.32, -19.76) * mm, v(103.56, -23.45) * mm, v(103.15, -28.5) * mm, v(103.96, -27.83) * mm, v(105.49, -26.26) * mm, v(107.65, -24.48) * mm, v(110.01, -22.92) * mm, v(111.17, -22.4) * mm, v(111.83, -22.84) * mm, v(111.5, -23.67) * mm, v(109.34, -25.22) * mm, v(107.29, -27) * mm, v(105.96, -28.27) * mm, v(104.18, -30.2) * mm, v(102.19, -32.6) * mm, v(100.75, -34.48) * mm, v(99.2, -33.76) * mm, v(98.59, -30.26) * mm, v(98.64, -26.55) * mm, v(99.2, -23.17) * mm, v(99.84, -20.6) * mm, v(99.65, -19.65) * mm, v(98.74, -19.6) * mm, v(97.07, -20.55) * mm, v(95.45, -22.27) * mm, v(93.82, -24.28) * mm, v(92.39, -26.57) * mm, v(91.43, -28.48) * mm, v(90.43, -31.4) * mm, v(89.71, -33.93) * mm, v(88.9, -34.55) * mm, v(87.9, -33.97) * mm, v(87.42, -31.35) * mm, v(87.37, -27.81) * mm, v(87.95, -23.04) * mm, v(88.62, -20.46) * mm, v(89.82, -16.85) * mm, v(91, -14.13) * mm, v(92.02, -12.23) * mm], "startDerivative": vector(-58.73, -135.62) * mm, "endDerivative": vector(52.61, 93.78) * mm});
            skFitSpline(sketch, "E180", {"points": [v(69.69, -29.46) * mm, v(69.82, -30.93) * mm, v(69.89, -32.24) * mm, v(70.9, -33.32) * mm, v(72.93, -34.13) * mm, v(75.9, -34.06) * mm, v(78, -33.59) * mm, v(79.63, -32.37) * mm, v(80.37, -30.61) * mm, v(79.87, -29.1) * mm, v(77.51, -26.95) * mm, v(76.79, -26.49) * mm, v(75.16, -24.8) * mm, v(73.88, -22.63) * mm, v(74.01, -20.26) * mm, v(75.43, -18.91) * mm, v(77.6, -17.5) * mm, v(80.37, -16.61) * mm, v(83.21, -16.34) * mm, v(85.72, -16.88) * mm, v(87.54, -18.37) * mm], "startDerivative": vector(5.07, -36.06) * mm, "endDerivative": vector(32.32, -32.5) * mm});
            skLineSegment(sketch, "E181", {"start": v(87.54, -18.37) * mm, "end": v(84.16, -21.82) * mm});
            skLineSegment(sketch, "E182", {"start": v(69.69, -29.46) * mm, "end": v(66.24, -31.83) * mm});
            skFitSpline(sketch, "E183", {"points": [v(66.24, -31.83) * mm, v(67.25, -33.12) * mm, v(68.94, -34.33) * mm, v(71.44, -35.28) * mm, v(74.7, -35.55) * mm, v(77.8, -35.28) * mm, v(80.86, -34.25) * mm, v(82.96, -32.93) * mm, v(84.38, -30.93) * mm, v(84.63, -28.25) * mm, v(83.01, -26.01) * mm, v(81.3, -24.33) * mm, v(79.83, -22.77) * mm, v(78.68, -21.21) * mm, v(78.55, -19.72) * mm, v(80.64, -18.44) * mm, v(82.67, -18.1) * mm, v(84.23, -18.32) * mm, v(84.9, -19.72) * mm, v(84.16, -21.82) * mm], "startDerivative": vector(20.7, -29.89) * mm, "endDerivative": vector(-19.13, -40.14) * mm});
            skFitSpline(sketch, "E184", {"points": [v(38.53, -16.74) * mm, v(35.91, -16.74) * mm, v(34.34, -17.72) * mm, v(33.69, -19.23) * mm, v(32.84, -21.32) * mm, v(32.12, -24.2) * mm, v(31.53, -27.54) * mm, v(31.4, -30.48) * mm, v(31.6, -32.97) * mm, v(32.64, -34.73) * mm, v(33.62, -34.4) * mm, v(34.93, -31.07) * mm, v(36.5, -27.47) * mm, v(38.27, -24.33) * mm, v(40.3, -21.9) * mm, v(42.65, -19.88) * mm, v(43.44, -19.49) * mm, v(42.91, -21.32) * mm, v(43.1, -23.35) * mm, v(44.22, -23.8) * mm, v(46.7, -23.48) * mm, v(46.84, -21.58) * mm, v(47.43, -19.36) * mm, v(48.54, -16.87) * mm, v(49.06, -16.35) * mm, v(45.2, -16.41) * mm, v(41.6, -18.57) * mm, v(39.31, -20.66) * mm, v(36.76, -23.94) * mm, v(36.96, -21.52) * mm, v(38.27, -17.79) * mm, v(38.53, -16.74) * mm]});
            skFitSpline(sketch, "E185", {"points": [v(55.8, -17.44) * mm, v(53.4, -17.59) * mm, v(52.08, -17.93) * mm, v(50.7, -19.36) * mm, v(49.92, -22.06) * mm, v(49.33, -24.56) * mm, v(48.89, -27.11) * mm, v(48.54, -29.47) * mm, v(48.35, -32.17) * mm, v(48.79, -34.23) * mm, v(49.87, -35.65) * mm, v(51.44, -35.3) * mm, v(52.81, -33.74) * mm, v(54.19, -31.92) * mm, v(56.3, -29.32) * mm, v(58.11, -26.87) * mm, v(59.68, -24.9) * mm, v(60.72, -23.58) * mm, v(60.62, -25.05) * mm, v(60.22, -27.3) * mm, v(60.03, -30.45) * mm, v(60.03, -32.76) * mm, v(60.67, -34.87) * mm, v(61.65, -35.85) * mm, v(64, -33.94) * mm, v(65.48, -32.51) * mm, v(66.12, -28.14) * mm, v(65.62, -28.78) * mm, v(64.64, -29.62) * mm, v(64.54, -27.6) * mm, v(64.99, -24.12) * mm, v(65.72, -21.66) * mm, v(66.75, -18.67) * mm, v(67.25, -17.63) * mm, v(64.53, -17.63) * mm, v(63.47, -18.26) * mm, v(62.14, -19.65) * mm, v(59.25, -23.2) * mm, v(54.57, -29.01) * mm, v(53.62, -30.02) * mm, v(53.06, -29.24) * mm, v(53.11, -27.17) * mm, v(53.84, -23.71) * mm, v(54.79, -20.7) * mm, v(55.4, -18.8) * mm, v(55.63, -18.19) * mm, v(55.8, -17.44) * mm]});
            skLineSegment(sketch, "E186", {"start": v(-64.75, -118.48) * mm, "end": v(-64.75, -126.88) * mm});
            skLineSegment(sketch, "E187", {"start": v(-64.75, -126.88) * mm, "end": v(-68.77, -121.77) * mm});
            skLineSegment(sketch, "E188", {"start": v(-68.77, -121.77) * mm, "end": v(-71.2, -121.77) * mm});
            skLineSegment(sketch, "E189", {"start": v(-71.2, -121.77) * mm, "end": v(-71.2, -127.74) * mm});
            skLineSegment(sketch, "E190", {"start": v(-71.2, -127.74) * mm, "end": v(-67.35, -127.74) * mm});
            skLineSegment(sketch, "E191", {"start": v(-64.75, -130.34) * mm, "end": v(-64.75, -150.38) * mm});
            skLineSegment(sketch, "E192", {"start": v(-66.7, -152.27) * mm, "end": v(-75.23, -152.27) * mm});
            skLineSegment(sketch, "E193", {"start": v(-75.23, -152.27) * mm, "end": v(-75.23, -140.83) * mm});
            skLineSegment(sketch, "E194", {"start": v(-75.23, -140.83) * mm, "end": v(-71.31, -148.84) * mm});
            skLineSegment(sketch, "E195", {"start": v(-71.31, -148.84) * mm, "end": v(-68.71, -148.84) * mm});
            skLineSegment(sketch, "E196", {"start": v(-68.71, -148.84) * mm, "end": v(-68.71, -131.22) * mm});
            skLineSegment(sketch, "E197", {"start": v(-68.71, -131.22) * mm, "end": v(-73.12, -131.22) * mm});
            skLineSegment(sketch, "E198", {"start": v(-75.16, -129.14) * mm, "end": v(-75.16, -120.37) * mm});
            skLineSegment(sketch, "E199", {"start": v(-64.75, -118.48) * mm, "end": v(-73.27, -118.48) * mm});
            skArc(sketch, "E200", {"start": v(-73.27, -118.48) * mm, "mid": v(-74.61, -119.03) * mm, "end": v(-75.16, -120.37) * mm});
            skArc(sketch, "E201", {"start": v(-75.16, -129.14) * mm, "mid": v(-74.57, -130.6) * mm, "end": v(-73.12, -131.22) * mm});
            skArc(sketch, "E202", {"start": v(-64.75, -130.34) * mm, "mid": v(-65.5, -128.5) * mm, "end": v(-67.35, -127.74) * mm});
            skArc(sketch, "E203", {"start": v(-66.7, -152.27) * mm, "mid": v(-65.33, -151.74) * mm, "end": v(-64.75, -150.38) * mm});
            skLineSegment(sketch, "E204", {"start": v(-56.82, -121.82) * mm, "end": v(-56.82, -148.94) * mm});
            skLineSegment(sketch, "E205", {"start": v(-56.82, -148.94) * mm, "end": v(-58.54, -152.3) * mm});
            skLineSegment(sketch, "E206", {"start": v(-58.54, -152.3) * mm, "end": v(-51.1, -152.3) * mm});
            skLineSegment(sketch, "E207", {"start": v(-51.1, -152.3) * mm, "end": v(-52.82, -149.02) * mm});
            skLineSegment(sketch, "E208", {"start": v(-52.82, -149.02) * mm, "end": v(-52.82, -121.86) * mm});
            skLineSegment(sketch, "E209", {"start": v(-52.82, -121.86) * mm, "end": v(-51.14, -121.86) * mm});
            skLineSegment(sketch, "E210", {"start": v(-51.14, -121.86) * mm, "end": v(-47.1, -127) * mm});
            skLineSegment(sketch, "E211", {"start": v(-47.1, -127) * mm, "end": v(-47.1, -118.47) * mm});
            skLineSegment(sketch, "E212", {"start": v(-47.1, -118.47) * mm, "end": v(-62.4, -118.47) * mm});
            skLineSegment(sketch, "E213", {"start": v(-62.4, -118.47) * mm, "end": v(-62.4, -127) * mm});
            skLineSegment(sketch, "E214", {"start": v(-62.4, -127) * mm, "end": v(-58.6, -121.82) * mm});
            skLineSegment(sketch, "E215", {"start": v(-58.6, -121.82) * mm, "end": v(-56.82, -121.82) * mm});
            skLineSegment(sketch, "E216", {"start": v(-44.98, -118.4) * mm, "end": v(-32.32, -118.4) * mm});
            skLineSegment(sketch, "E217", {"start": v(-32.32, -118.4) * mm, "end": v(-32.32, -126.95) * mm});
            skLineSegment(sketch, "E218", {"start": v(-32.32, -126.95) * mm, "end": v(-36.41, -121.78) * mm});
            skLineSegment(sketch, "E219", {"start": v(-36.41, -121.78) * mm, "end": v(-39.18, -121.78) * mm});
            skLineSegment(sketch, "E220", {"start": v(-39.18, -121.78) * mm, "end": v(-39.18, -127.84) * mm});
            skLineSegment(sketch, "E221", {"start": v(-39.18, -127.84) * mm, "end": v(-36.43, -127.84) * mm});
            skLineSegment(sketch, "E222", {"start": v(-36.43, -127.84) * mm, "end": v(-36.37, -131.22) * mm});
            skLineSegment(sketch, "E223", {"start": v(-36.37, -131.22) * mm, "end": v(-39.1, -131.22) * mm});
            skLineSegment(sketch, "E224", {"start": v(-39.1, -131.22) * mm, "end": v(-39.1, -148.79) * mm});
            skLineSegment(sketch, "E225", {"start": v(-39.1, -148.79) * mm, "end": v(-36.41, -148.79) * mm});
            skLineSegment(sketch, "E226", {"start": v(-36.41, -148.79) * mm, "end": v(-32.32, -140.82) * mm});
            skLineSegment(sketch, "E227", {"start": v(-32.32, -140.82) * mm, "end": v(-32.32, -152.25) * mm});
            skLineSegment(sketch, "E228", {"start": v(-32.32, -152.25) * mm, "end": v(-44.94, -152.25) * mm});
            skLineSegment(sketch, "E229", {"start": v(-44.94, -152.25) * mm, "end": v(-43.23, -148.78) * mm});
            skLineSegment(sketch, "E230", {"start": v(-43.23, -148.78) * mm, "end": v(-43.23, -121.8) * mm});
            skLineSegment(sketch, "E231", {"start": v(-43.23, -121.8) * mm, "end": v(-44.98, -118.4) * mm});
            skLineSegment(sketch, "E232.bottom", {"start": v(-24.55, -121.9) * mm, "end": v(-21.65, -121.9) * mm});
            skLineSegment(sketch, "E232.top", {"start": v(-24.55, -127.8) * mm, "end": v(-21.65, -127.8) * mm});
            skLineSegment(sketch, "E232.left", {"start": v(-24.55, -121.9) * mm, "end": v(-24.55, -127.8) * mm});
            skLineSegment(sketch, "E232.right", {"start": v(-21.65, -121.9) * mm, "end": v(-21.65, -127.8) * mm});
            skLineSegment(sketch, "E233.bottom", {"start": v(34.1, -125.11) * mm, "end": v(36.93, -125.11) * mm});
            skLineSegment(sketch, "E233.top", {"start": v(34.1, -148.9) * mm, "end": v(36.93, -148.9) * mm});
            skLineSegment(sketch, "E233.left", {"start": v(34.1, -125.11) * mm, "end": v(34.1, -148.9) * mm});
            skLineSegment(sketch, "E233.right", {"start": v(36.93, -125.11) * mm, "end": v(36.93, -148.9) * mm});
            skLineSegment(sketch, "E234.top", {"start": v(12.81, -148.9) * mm, "end": v(15.66, -148.9) * mm});
            skLineSegment(sketch, "E234.left", {"start": v(12.81, -121.47) * mm, "end": v(12.81, -148.9) * mm});
            skLineSegment(sketch, "E234.right", {"start": v(15.66, -121.47) * mm, "end": v(15.66, -148.9) * mm});
            skLineSegment(sketch, "E235.top", {"start": v(19.57, -148.9) * mm, "end": v(22.4, -148.9) * mm});
            skLineSegment(sketch, "E235.left", {"start": v(19.57, -121.47) * mm, "end": v(19.57, -148.9) * mm});
            skLineSegment(sketch, "E235.right", {"start": v(22.4, -121.47) * mm, "end": v(22.4, -148.9) * mm});
            skLineSegment(sketch, "E236", {"start": v(15.66, -121.47) * mm, "end": v(19.57, -121.47) * mm});
            skLineSegment(sketch, "E237.bottom", {"start": v(-9.07, -121.8) * mm, "end": v(-6.06, -121.8) * mm});
            skLineSegment(sketch, "E237.left", {"start": v(-9.07, -121.8) * mm, "end": v(-9.07, -152.3) * mm});
            skLineSegment(sketch, "E237.right", {"start": v(-6.06, -121.8) * mm, "end": v(-6.06, -152.3) * mm});
            skLineSegment(sketch, "E238.top", {"start": v(-2.02, -121.8) * mm, "end": v(0.85, -121.8) * mm});
            skLineSegment(sketch, "E238.left", {"start": v(-2.02, -152.3) * mm, "end": v(-2.02, -121.8) * mm});
            skLineSegment(sketch, "E238.right", {"start": v(0.85, -152.3) * mm, "end": v(0.85, -121.8) * mm});
            skLineSegment(sketch, "E239", {"start": v(-6.06, -152.3) * mm, "end": v(-2.02, -152.3) * mm});
            skLineSegment(sketch, "E240.bottom", {"start": v(-24.58, -131.27) * mm, "end": v(-21.7, -131.27) * mm});
            skLineSegment(sketch, "E240.left", {"start": v(-24.58, -131.27) * mm, "end": v(-24.58, -152.25) * mm});
            skLineSegment(sketch, "E240.right", {"start": v(-21.7, -131.27) * mm, "end": v(-21.7, -152.3) * mm});
            skLineSegment(sketch, "E241", {"start": v(-24.58, -152.25) * mm, "end": v(-30.36, -152.25) * mm});
            skLineSegment(sketch, "E242", {"start": v(-30.36, -152.25) * mm, "end": v(-28.66, -148.88) * mm});
            skLineSegment(sketch, "E243", {"start": v(-28.66, -148.88) * mm, "end": v(-28.66, -120.44) * mm});
            skLineSegment(sketch, "E244", {"start": v(-26.85, -118.49) * mm, "end": v(-19.64, -118.49) * mm});
            skLineSegment(sketch, "E245", {"start": v(-17.68, -120.18) * mm, "end": v(-17.68, -148.8) * mm});
            skLineSegment(sketch, "E246", {"start": v(-17.68, -148.8) * mm, "end": v(-15.95, -152.3) * mm});
            skLineSegment(sketch, "E247", {"start": v(-15.95, -152.3) * mm, "end": v(-21.7, -152.3) * mm});
            skArc(sketch, "E248", {"start": v(-26.85, -118.49) * mm, "mid": v(-28.18, -119.07) * mm, "end": v(-28.66, -120.44) * mm});
            skArc(sketch, "E249", {"start": v(-17.68, -120.18) * mm, "mid": v(-18.34, -118.97) * mm, "end": v(-19.64, -118.49) * mm});
            skLineSegment(sketch, "E250", {"start": v(-9.07, -152.3) * mm, "end": v(-14.92, -152.3) * mm});
            skLineSegment(sketch, "E251", {"start": v(-14.92, -152.3) * mm, "end": v(-13.12, -149.28) * mm});
            skLineSegment(sketch, "E252", {"start": v(-13.12, -149.28) * mm, "end": v(-13.12, -121.6) * mm});
            skLineSegment(sketch, "E253", {"start": v(-13.12, -121.6) * mm, "end": v(-14.66, -118.7) * mm});
            skLineSegment(sketch, "E254", {"start": v(-14.66, -118.7) * mm, "end": v(1.74, -118.7) * mm});
            skLineSegment(sketch, "E255", {"start": v(0.85, -152.3) * mm, "end": v(6.81, -152.3) * mm});
            skLineSegment(sketch, "E256", {"start": v(6.81, -152.3) * mm, "end": v(4.83, -148.96) * mm});
            skLineSegment(sketch, "E257", {"start": v(4.83, -148.96) * mm, "end": v(4.83, -121.47) * mm});
            skArc(sketch, "E258", {"start": v(4.83, -121.47) * mm, "mid": v(3.9, -119.4) * mm, "end": v(1.74, -118.7) * mm});
            skLineSegment(sketch, "E259", {"start": v(12.81, -121.47) * mm, "end": v(7.18, -121.47) * mm});
            skLineSegment(sketch, "E260", {"start": v(7.18, -121.47) * mm, "end": v(8.96, -124.81) * mm});
            skLineSegment(sketch, "E261", {"start": v(8.96, -124.81) * mm, "end": v(8.96, -150.44) * mm});
            skLineSegment(sketch, "E262", {"start": v(10.97, -152.34) * mm, "end": v(24.26, -152.34) * mm});
            skLineSegment(sketch, "E263", {"start": v(26.48, -150.25) * mm, "end": v(26.48, -124.72) * mm});
            skLineSegment(sketch, "E264", {"start": v(26.48, -124.72) * mm, "end": v(27.95, -121.47) * mm});
            skLineSegment(sketch, "E265", {"start": v(27.95, -121.47) * mm, "end": v(22.4, -121.47) * mm});
            skArc(sketch, "E266", {"start": v(8.96, -150.44) * mm, "mid": v(9.59, -151.8) * mm, "end": v(10.97, -152.34) * mm});
            skArc(sketch, "E267", {"start": v(24.26, -152.34) * mm, "mid": v(25.82, -151.77) * mm, "end": v(26.48, -150.25) * mm});
            skLineSegment(sketch, "E268.bottom", {"start": v(32.02, -121.47) * mm, "end": v(38.9, -121.47) * mm});
            skLineSegment(sketch, "E268.top", {"start": v(32.02, -152.34) * mm, "end": v(38.9, -152.34) * mm});
            skLineSegment(sketch, "E268.left", {"start": v(30.12, -123.38) * mm, "end": v(30.12, -150.44) * mm});
            skLineSegment(sketch, "E268.right", {"start": v(40.8, -123.38) * mm, "end": v(40.8, -150.44) * mm});
            skArc(sketch, "E269", {"start": v(32.02, -121.47) * mm, "mid": v(30.67, -122.03) * mm, "end": v(30.12, -123.38) * mm});
            skArc(sketch, "E270", {"start": v(40.8, -123.38) * mm, "mid": v(40.24, -122.03) * mm, "end": v(38.9, -121.47) * mm});
            skArc(sketch, "E271", {"start": v(30.12, -150.44) * mm, "mid": v(30.67, -151.79) * mm, "end": v(32.02, -152.34) * mm});
            skArc(sketch, "E272", {"start": v(38.9, -152.34) * mm, "mid": v(40.24, -151.79) * mm, "end": v(40.8, -150.44) * mm});
            skPoint(sketch, "E273.orphan", {"position": v(30.12, -121.47) * mm});
            skPoint(sketch, "E274.orphan", {"position": v(30.12, -152.34) * mm});
            skLineSegment(sketch, "E275", {"start": v(44.24, -125) * mm, "end": v(44.24, -148.98) * mm});
            skLineSegment(sketch, "E276", {"start": v(44.24, -148.98) * mm, "end": v(42.47, -152.34) * mm});
            skLineSegment(sketch, "E277", {"start": v(42.47, -152.34) * mm, "end": v(49.79, -152.34) * mm});
            skLineSegment(sketch, "E278", {"start": v(49.79, -152.34) * mm, "end": v(48.13, -149.2) * mm});
            skLineSegment(sketch, "E279", {"start": v(48.13, -149.2) * mm, "end": v(48.13, -124.94) * mm});
            skLineSegment(sketch, "E280", {"start": v(48.13, -124.94) * mm, "end": v(50.58, -124.94) * mm});
            skLineSegment(sketch, "E281", {"start": v(50.58, -124.94) * mm, "end": v(54.4, -128.27) * mm});
            skLineSegment(sketch, "E282", {"start": v(54.4, -128.27) * mm, "end": v(54.4, -123.53) * mm});
            skLineSegment(sketch, "E283", {"start": v(44.24, -125) * mm, "end": v(42.45, -121.63) * mm});
            skLineSegment(sketch, "E284", {"start": v(42.45, -121.63) * mm, "end": v(52.49, -121.63) * mm});
            skArc(sketch, "E285", {"start": v(54.4, -123.53) * mm, "mid": v(53.84, -122.19) * mm, "end": v(52.49, -121.63) * mm});
            skLineSegment(sketch, "E286.bottom", {"start": v(60.64, -134) * mm, "end": v(63.63, -134) * mm});
            skLineSegment(sketch, "E286.left", {"start": v(60.64, -134) * mm, "end": v(60.64, -152.34) * mm});
            skLineSegment(sketch, "E286.right", {"start": v(63.63, -134) * mm, "end": v(63.63, -152.34) * mm});
            skLineSegment(sketch, "E287.top", {"start": v(60.63, -130.53) * mm, "end": v(63.6, -130.53) * mm});
            skLineSegment(sketch, "E287.left", {"start": v(60.63, -119.33) * mm, "end": v(60.63, -130.53) * mm});
            skLineSegment(sketch, "E287.right", {"start": v(63.6, -121.5) * mm, "end": v(63.6, -130.53) * mm});
            skLineSegment(sketch, "E288", {"start": v(60.64, -152.34) * mm, "end": v(54.87, -152.34) * mm});
            skLineSegment(sketch, "E289", {"start": v(54.87, -152.34) * mm, "end": v(56.8, -148.9) * mm});
            skLineSegment(sketch, "E290", {"start": v(56.8, -148.9) * mm, "end": v(56.8, -122.63) * mm});
            skLineSegment(sketch, "E291", {"start": v(56.8, -122.63) * mm, "end": v(55.06, -119.33) * mm});
            skLineSegment(sketch, "E292", {"start": v(55.06, -119.33) * mm, "end": v(60.63, -119.33) * mm});
            skLineSegment(sketch, "E293", {"start": v(63.6, -121.5) * mm, "end": v(69.35, -121.5) * mm});
            skLineSegment(sketch, "E294", {"start": v(69.35, -121.5) * mm, "end": v(67.35, -125.1) * mm});
            skLineSegment(sketch, "E295", {"start": v(67.35, -125.1) * mm, "end": v(67.35, -130.83) * mm});
            skLineSegment(sketch, "E296", {"start": v(63.63, -152.34) * mm, "end": v(69.27, -152.34) * mm});
            skLineSegment(sketch, "E297", {"start": v(69.27, -152.34) * mm, "end": v(67.35, -148.68) * mm});
            skLineSegment(sketch, "E298", {"start": v(67.35, -148.68) * mm, "end": v(67.35, -134.04) * mm});
            skArc(sketch, "E299", {"start": v(65.22, -132.12) * mm, "mid": v(66.48, -131.8) * mm, "end": v(67.35, -130.83) * mm});
            skArc(sketch, "E300", {"start": v(67.35, -134.04) * mm, "mid": v(66.7, -132.67) * mm, "end": v(65.22, -132.32) * mm});
            skLineSegment(sketch, "E301", {"start": v(65.22, -132.12) * mm, "end": v(65.22, -132.32) * mm});
            skLineSegment(sketch, "E302", {"start": v(80.46, -121.47) * mm, "end": v(80.46, -128.27) * mm});
            skLineSegment(sketch, "E303", {"start": v(80.46, -128.27) * mm, "end": v(76.53, -124.82) * mm});
            skLineSegment(sketch, "E304", {"start": v(76.53, -124.82) * mm, "end": v(74.6, -124.82) * mm});
            skLineSegment(sketch, "E305", {"start": v(74.6, -124.82) * mm, "end": v(74.6, -128.35) * mm});
            skLineSegment(sketch, "E306", {"start": v(74.6, -128.35) * mm, "end": v(78.53, -128.35) * mm});
            skLineSegment(sketch, "E307", {"start": v(80.46, -130.02) * mm, "end": v(80.46, -150.53) * mm});
            skLineSegment(sketch, "E308", {"start": v(78.75, -152.34) * mm, "end": v(70.69, -152.34) * mm});
            skLineSegment(sketch, "E309", {"start": v(70.69, -152.34) * mm, "end": v(70.69, -144.7) * mm});
            skLineSegment(sketch, "E310", {"start": v(70.69, -144.7) * mm, "end": v(74.58, -148.85) * mm});
            skLineSegment(sketch, "E311", {"start": v(74.58, -148.85) * mm, "end": v(76.53, -148.85) * mm});
            skLineSegment(sketch, "E312", {"start": v(76.53, -148.85) * mm, "end": v(76.53, -131.67) * mm});
            skLineSegment(sketch, "E313", {"start": v(76.53, -131.67) * mm, "end": v(72.54, -131.67) * mm});
            skLineSegment(sketch, "E314", {"start": v(70.67, -129.37) * mm, "end": v(70.67, -123.29) * mm});
            skLineSegment(sketch, "E315", {"start": v(80.46, -121.47) * mm, "end": v(72.75, -121.47) * mm});
            skArc(sketch, "E316", {"start": v(72.75, -121.47) * mm, "mid": v(71.36, -121.99) * mm, "end": v(70.67, -123.29) * mm});
            skArc(sketch, "E317", {"start": v(70.67, -129.37) * mm, "mid": v(71.2, -130.85) * mm, "end": v(72.54, -131.67) * mm});
            skArc(sketch, "E318", {"start": v(80.46, -130.02) * mm, "mid": v(79.88, -128.74) * mm, "end": v(78.53, -128.35) * mm});
            skArc(sketch, "E319", {"start": v(78.75, -152.34) * mm, "mid": v(79.97, -151.78) * mm, "end": v(80.46, -150.53) * mm});
            skFitSpline(sketch, "E320", {"points": [v(11.85, -55.26) * mm, v(24.77, -58.88) * mm, v(41.66, -57.7) * mm, v(55.13, -54.2) * mm, v(69.36, -52.67) * mm, v(85.93, -55.1) * mm], "startDerivative": vector(79.06, -22.21) * mm, "endDerivative": vector(78.5, -14.75) * mm});
            skFitSpline(sketch, "E321", {"points": [v(85.93, -55.1) * mm, v(78.49, -58.67) * mm, v(66.96, -67) * mm], "startDerivative": vector(-16.55, -6.88) * mm, "endDerivative": vector(-21.2, -16.5) * mm});
            skFitSpline(sketch, "E322", {"points": [v(66.96, -67) * mm, v(79.31, -78.4) * mm, v(85.93, -87.69) * mm], "startDerivative": vector(24.68, -20.87) * mm, "endDerivative": vector(12.89, -20.49) * mm});
            skFitSpline(sketch, "E323", {"points": [v(85.93, -87.69) * mm, v(77.33, -85.26) * mm, v(56.8, -86.16) * mm, v(37.83, -89.94) * mm, v(21.3, -90.66) * mm, v(11.76, -87.69) * mm], "startDerivative": vector(-48.13, 18.53) * mm, "endDerivative": vector(-53.64, 20.5) * mm});
            skLineSegment(sketch, "E324", {"start": v(11.84, -59.67) * mm, "end": v(11.82, -66.79) * mm});
            skFitSpline(sketch, "E325", {"points": [v(11.84, -59.67) * mm, v(31.89, -62.64) * mm, v(57.56, -57.6) * mm, v(72.6, -56.25) * mm, v(81.05, -57.27) * mm], "startDerivative": vector(41.85, -22.44) * mm, "endDerivative": vector(45.36, -7.33) * mm});
            skFitSpline(sketch, "E326", {"points": [v(11.82, -66.79) * mm, v(31.89, -70.66) * mm, v(57.38, -65.44) * mm, v(71.7, -63.36) * mm], "startDerivative": vector(28.9, -20.43) * mm, "endDerivative": vector(40.09, 4.16) * mm});
            skFitSpline(sketch, "E327", {"points": [v(11.8, -74.71) * mm, v(21.08, -77.78) * mm, v(34.05, -77.96) * mm, v(62.96, -71.56) * mm, v(70.97, -70.42) * mm], "startDerivative": vector(44.32, -16.94) * mm, "endDerivative": vector(33.66, 2.92) * mm});
            skFitSpline(sketch, "E328", {"points": [v(11.77, -82.64) * mm, v(24.14, -86.15) * mm, v(40.09, -84.53) * mm, v(68.9, -79.04) * mm, v(80.4, -79.7) * mm], "startDerivative": vector(49.9, -22.62) * mm, "endDerivative": vector(53.57, -6.12) * mm});
            skLineSegment(sketch, "E329", {"start": v(11.85, -55.26) * mm, "end": v(11.85, -52.2) * mm});
            skLineSegment(sketch, "E330", {"start": v(11.85, -52.2) * mm, "end": v(7.75, -52.19) * mm});
            skLineSegment(sketch, "E331", {"start": v(7.75, -52.19) * mm, "end": v(7.75, -61.72) * mm});
            skLineSegment(sketch, "E332", {"start": v(7.75, -61.72) * mm, "end": v(4.24, -61.71) * mm});
            skLineSegment(sketch, "E333", {"start": v(4.24, -61.71) * mm, "end": v(4.24, -51.93) * mm});
            skLineSegment(sketch, "E334", {"start": v(4.24, -51.93) * mm, "end": v(-2.97, -51.9) * mm});
            skLineSegment(sketch, "E335", {"start": v(-2.97, -51.9) * mm, "end": v(-2.97, -62.8) * mm});
            skLineSegment(sketch, "E336", {"start": v(-2.97, -62.8) * mm, "end": v(-6.16, -62.8) * mm});
            skLineSegment(sketch, "E337", {"start": v(-6.16, -62.8) * mm, "end": v(-6.16, -52.12) * mm});
            skLineSegment(sketch, "E338", {"start": v(-6.16, -52.12) * mm, "end": v(-19.13, -52.08) * mm});
            skLineSegment(sketch, "E339", {"start": v(-19.13, -52.08) * mm, "end": v(-19.18, -63.28) * mm});
            skLineSegment(sketch, "E340", {"start": v(-19.18, -63.28) * mm, "end": v(-22.78, -63.27) * mm});
            skLineSegment(sketch, "E341", {"start": v(-22.78, -63.27) * mm, "end": v(-22.78, -52.37) * mm});
            skLineSegment(sketch, "E342", {"start": v(-22.78, -52.37) * mm, "end": v(-29.54, -52.37) * mm});
            skLineSegment(sketch, "E343", {"start": v(-29.54, -52.37) * mm, "end": v(-29.54, -61.72) * mm});
            skLineSegment(sketch, "E344", {"start": v(-29.54, -61.72) * mm, "end": v(-32.51, -61.71) * mm});
            skLineSegment(sketch, "E345", {"start": v(-32.51, -61.71) * mm, "end": v(-32.51, -52.37) * mm});
            skLineSegment(sketch, "E346", {"start": v(-32.51, -52.37) * mm, "end": v(-37.24, -52.37) * mm});
            skLineSegment(sketch, "E347", {"start": v(-37.24, -52.37) * mm, "end": v(-36.93, -87.69) * mm});
            skLineSegment(sketch, "E348", {"start": v(-36.93, -87.69) * mm, "end": v(-12.38, -101.36) * mm});
            skLineSegment(sketch, "E349", {"start": v(-10.34, -100.2) * mm, "end": v(11.76, -87.69) * mm});
            skLineSegment(sketch, "E350", {"start": v(-12.38, -101.36) * mm, "end": v(-12.38, -63.71) * mm});
            skLineSegment(sketch, "E351", {"start": v(-12.38, -63.71) * mm, "end": v(-10.34, -63.71) * mm});
            skLineSegment(sketch, "E352", {"start": v(-10.34, -63.71) * mm, "end": v(-10.34, -100.2) * mm});
            skLineSegment(sketch, "E353", {"start": v(-31.84, -85.3) * mm, "end": v(-21.2, -91.23) * mm});
            skLineSegment(sketch, "E354", {"start": v(-4.46, -73.97) * mm, "end": v(-4.46, -90.15) * mm});
            skLineSegment(sketch, "E355", {"start": v(-4.46, -90.15) * mm, "end": v(5.81, -85.46) * mm});
            skLineSegment(sketch, "E356", {"start": v(5.81, -85.46) * mm, "end": v(5.81, -73.25) * mm});
            skLineSegment(sketch, "E357", {"start": v(-31.84, -85.3) * mm, "end": v(-31.84, -72.9) * mm});
            skLineSegment(sketch, "E358", {"start": v(-21.2, -91.23) * mm, "end": v(-21.2, -73.98) * mm});
            skArc(sketch, "E359", {"start": v(-21.2, -73.98) * mm, "mid": v(-25.92, -67.56) * mm, "end": v(-31.84, -72.9) * mm});
            skArc(sketch, "E360", {"start": v(5.81, -73.25) * mm, "mid": v(0.3, -68.1) * mm, "end": v(-4.46, -73.97) * mm});
            skLineSegment(sketch, "E361.trimOffspring", {"start": v(11.8, -74.71) * mm, "end": v(11.77, -82.64) * mm});
            skSolve(sketch);
        }
        {
            var Q0;
            Q0 = qSketchRegion(id + "F4", true);
            extrude(context, id + "F5", {"entities" : qUnion([Q0]), "operationType" : NewBodyOperationType.REMOVE, "oppositeDirection" : true, "depth" : 2.54 * mm, "offsetDistance" : 25.4 * mm});
        }
        {
            var Q0;
            Q0=makeQuery(id+"F1.opExtrude","CAP_EDGE",EDGE,{"disambiguationData":[OSD([sQuery(id+"F0.wireOp",EDGE,"E1")])],"isStart":false});
            var Q1;
            Q1=makeQuery(id+"F1.opExtrude","CAP_EDGE",EDGE,{"disambiguationData":[OSD([sQuery(id+"F0.wireOp",EDGE,"E13")])],"isStart":false});
            var Q2;
            Q2=makeQuery(id+"F1.opExtrude","CAP_EDGE",EDGE,{"disambiguationData":[OSD([sQuery(id+"F0.wireOp",EDGE,"E15")])],"isStart":false});
            var Q3;
            Q3=makeQuery(id+"F1.opExtrude","CAP_EDGE",EDGE,{"disambiguationData":[OSD([sQuery(id+"F0.wireOp",EDGE,"E0.right")])],"isStart":false});
            var Q4;
            Q4=makeQuery(id+"F1.opExtrude","CAP_EDGE",EDGE,{"disambiguationData":[OSD([sQuery(id+"F0.wireOp",EDGE,"E7.MirrorCS")])],"isStart":false});
            var Q5;
            Q5=makeQuery(id+"F1.opExtrude","CAP_EDGE",EDGE,{"disambiguationData":[OSD([sQuery(id+"F0.wireOp",EDGE,"E0.left")])],"isStart":false});
            var Q6;
            Q6=makeQuery(id+"F1.opExtrude","CAP_EDGE",EDGE,{"disambiguationData":[OSD([sQuery(id+"F0.wireOp",EDGE,"E16.MirrorCS")])],"isStart":false});
            var Q7;
            Q7=makeQuery(id+"F1.opExtrude","CAP_EDGE",EDGE,{"disambiguationData":[OSD([sQuery(id+"F0.wireOp",EDGE,"E3.MirrorCS")])],"isStart":false});
            chamfer(context, id + "F6", {"entities" : qUnion([Q0, Q1, Q2, Q3, Q4, Q5, Q6, Q7]), "chamferType" : ChamferType.OFFSET_ANGLE, "width" : 5.08 * mm, "oppositeDirection" : false, "angle" : 45 * degree, "tangentPropagation" : true});
        }
    });